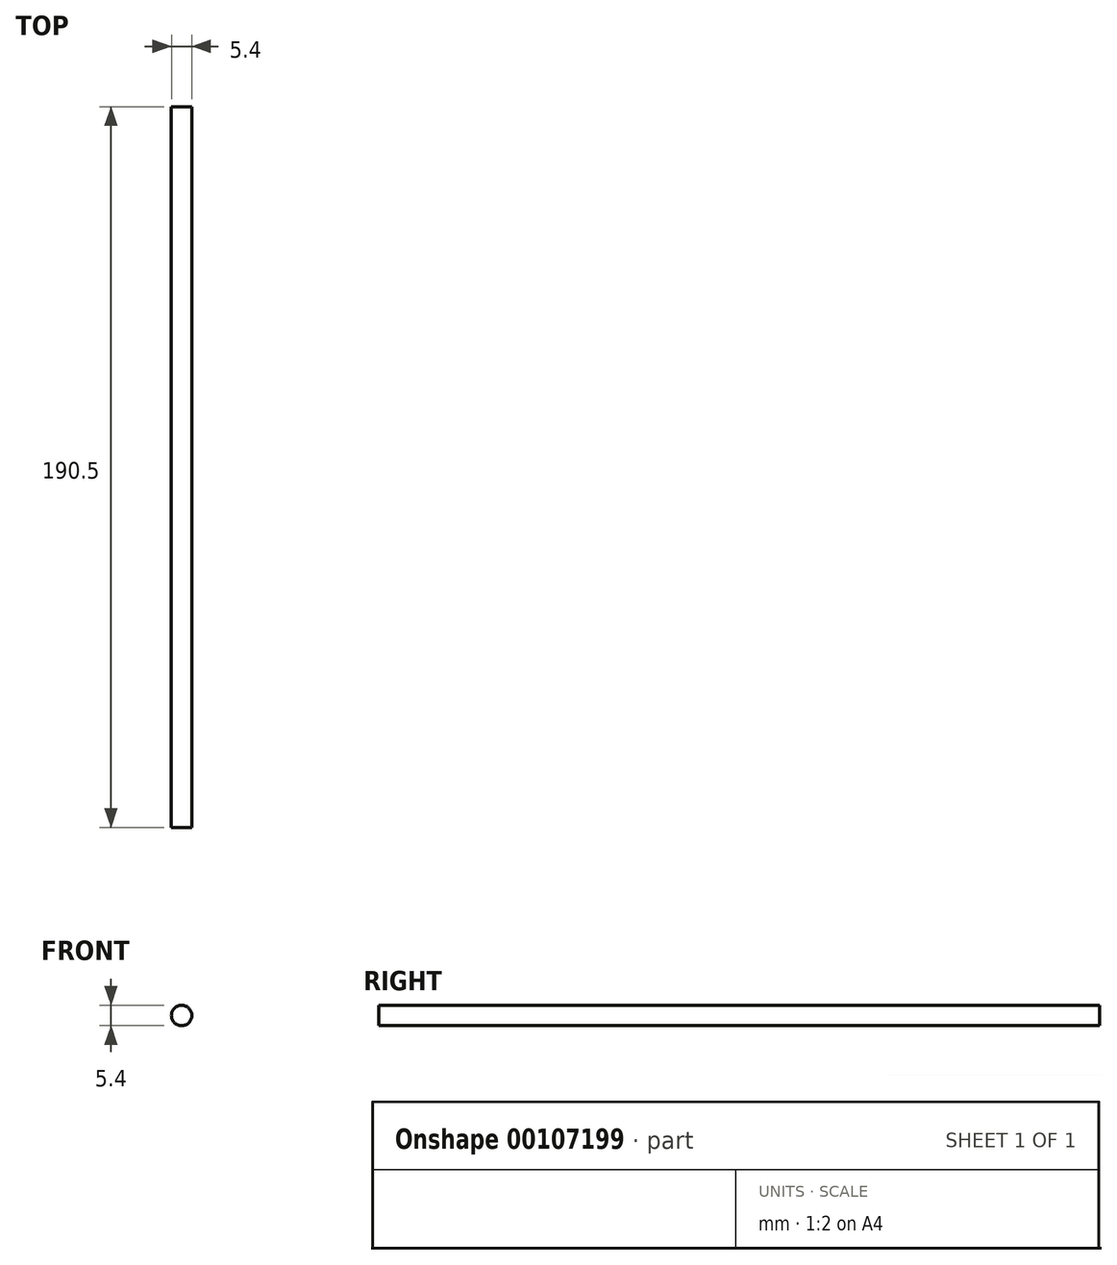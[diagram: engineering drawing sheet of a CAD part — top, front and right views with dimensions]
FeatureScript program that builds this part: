
annotation { "Feature Type Name" : "Feature", "Feature Type Description" : "" }
export const myFeature = defineFeature(function(context is Context, id is Id, definition is map)
    precondition{}
    {
        {
            var Q0;
            Q0=qCreatedBy(makeId("Front.planeOp"),FACE);
            var sketch = newSketch(context, id + "F0", { "sketchPlane" : qUnion([Q0])});
            skPoint(sketch, "E0", {"position": v(-71.34, 27.66) * mm});
            skCircle(sketch, "E1", {"center": v(-71.34, 27.66) * mm, "radius": 2.7 * mm});
            skSolve(sketch);
        }
        {
            var Q0;
            Q0=makeQuery(id+"F0.imprint","IMPRINT",FACE,{"disambiguationData":[TD([[makeQuery(id+"F0.imprint","IMPRINT",EDGE,{"derivedFrom":sQuery(id+"F0.wireOp",EDGE,"E1")}),1.0]])]});
            extrude(context, id + "F1", {"entities" : qUnion([Q0]), "depth" : 190.5 * mm});
        }
    });
